# Revit family: PRE080015-FR
name_source: partatom
category: Appareils sanitaires
revit_build: Autodesk Revit 2017 (Build: 20160225_1515(x64)
units: mm (PartAtom-declared; Revit-internal decimal feet)

## family parameters
Basée sur le plan de construction = Non
Cote de connecteur circulaire = Utiliser le diamètre
Couper avec des vides une fois chargée = Non
Partagée = Non
Point de calcul de pièce = Non
Toujours verticalement = Oui
Type d'élément = Normal

## types (1)
- 70806 PRESTO CHEF Mélangeur mural avec bec par-dessous
    Adresse = 7, RUE RACINE - 92542 MONTROUGE CEDEX FRANCE
    Debit = 3 l/min par limiteur de débit intégré

Aérateur anti-tartre haute qualité

Dispositif anti-coup de bélier
    Description = Produit résistant à un usage intensif
Interface corps/bec renforcé avec double paliers de glissement : absence de jeu et endurance élevée
Bec cossu : diamètre 22 mm
Volants intuitifs et ergonomiques : facilité de préhension
Hygiène : bec à intérieur lisse
Version murale : facilite le nettoyage et favorise une hygiène optimale
Facilité de nettoyage
Bec haut pour laisser passer les grands contenants
Maintenance aisée : présence d'une fente sous la pastille rouge/bleue permettant le passage d'un tournevis
Facilité de maintenance : disponibilité de toutes les pièces d'usure
Brise-jet pour canaliser l'eau et éviter les projections d'eau latérales
    Diamètre Nominal = 15 mm  [stored 0.0492126 ft]
    Edition number = 0
    Fabricant = LES ROBINETS PRESTO S.A.
    Finition = Corps en laiton chromé conforme aux normes NF EN1982/ NF EN 12164 / NF EN 12165
Traitement de surface Nickel-Chrome selon NF EN12540
Résistance au brouillard salin neutre (NSS) : 200 h selon NF ISO 9229
    Flux = 0.1 L/s
    Fonction = Bec orientable à 360°, saillie 300 mm, hauteur sous"corps" 182 mm, diamètre 22 mm. Epaisseur de bec : 1,5 mm.
Tête céramique 1/4 de tour avec débit 30L/min à 3 bar
Brise-jet anti-tartre interchangeable

Pression d'utilisation recommandée : 1 à 5 bars

Débit : 30L/min à 3 bar

Alimentation hydraulique : Raccords excentrés M 1/2'' M 3/4'' fournis avec rosaces

Matière et couleur de finition : 
Corps et bec en laiton chromé
Matière conforme avec la liste "UBA"

Résistance thermique : Résiste à une température de 75° C durant 30 minutes (dans le cadre de chocs thermiques).
    HC = 25 mm  [stored 0.082021 ft]
    Hauteur = 215 mm  [stored 0.705381 ft]
    Largeur = 217 mm  [stored 0.711942 ft]
    Lien CCTP = http://www.prestodatashare.com
    Lien fiche produit = http://www.prestodatashare.com
    Lien notice d'utilisation = http://www.prestodatashare.com
    Matériau = Laiton poli chromé
    Modèle = 70806 PRESTO CHEF Mélangeur mural avec bec par-dessous
    Perte de charge = 0.0 Pa
    Polantis code = PRE080015
    Product Guid = 4cf46d49-1ff3-4e6b-a9ef-2af74d86712c
    Product data url = https://www.bimobject.com
    Profondeur = 374 mm  [stored 1.22703 ft]
    Raccordement = 2xG1/2 entraxe 150 derriere haut
    Reference = 70806
    URL = http://www.prestodatashare.com
    URL Fabricant = http://www.prestodatashare.com
    Variantes = 70806

note: [stored X ft] marks values corroborated as IEEE doubles in the binary element streams (Revit-internal decimal feet)
